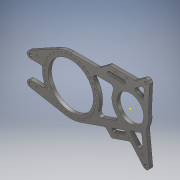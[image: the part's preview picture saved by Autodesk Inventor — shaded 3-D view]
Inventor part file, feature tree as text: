
AUTODESK INVENTOR PART (.ipt)
format: ipt  version: 2019 (Build 230136000, 136)  size: 542,208 bytes
history: native  units: in
note: dims shown in document units (in); Inventor stores cm internally (conversion verified against a paired STEP export)
features: sketch x20, extrude x14, hole x5, fillet x2, chamfer x1, projected_geometry x1
ambient origin geometry x8: Origin, YZ Plane, XZ Plane, XY Plane, X Axis, Y Axis, Z Axis, Center Point
bodies: Body1 (feature_tree)
feature tree (43):
  extrude  "Extrusion13"  Depth=0.5in TaperAngle=0.0deg
  hole  "Hole4"  [1 undecoded]
  extrude  "Extrusion14"  Depth=0.5in TaperAngle=0.0deg
  extrude  "Extrusion15"  Depth=5.0in
  extrude  "Extrusion16"  Depth=1.0in
  hole  "Hole6"  [1 undecoded]
  extrude  "Extrusion17"  Depth=0.5in TaperAngle=0.0deg
  hole  "Hole7"  [1 undecoded]
  hole  "Hole9"  [1 undecoded]
  hole  "Hole10"  [1 undecoded]
  extrude  "Extrusion18"  Depth=1.0in
  extrude  "Extrusion19"  Depth=1.0in
  sketch  "Sketch33"  dims[d183=0.257in d184=0.75in d185=0.438in d186=0.25in d187=0.5635in d188=1.0in d189=0.8108in d191=1.0in]
  extrude  "Extrusion21"  Depth=0.239in
  extrude  "Extrusion22"  Depth=0.5in
  extrude  "Extrusion23"  Depth=1.0in
  extrude  "Extrusion24"  Depth=0.75in
  fillet  "Fillet2"  Radius=0.75in
  extrude  "Extrusion25"  Depth=0.25in
  extrude  "Extrusion26"  Depth=1.0in TaperAngle=0.0deg
  fillet  "Fillet3"  Radius=0.25in
  extrude  "Extrusion27"  Depth=1.0in TaperAngle=0.0deg
  chamfer  "Chamfer1"  Distance=0.75in
  sketch  "Sketch40"  dims[d214=0.5in d215=1.0in d216=0.0in d217=0.25in d218=1.0in d219=0.0in d220=0.75in d221=0.5in d223=0.75in d231=0.25in d232=1.0in d233=0.0in d234=0.25in d235=1.0in d236=0.0in d237=0.75in d238=1.0in d239=0.0in d240=0.5in d241=0.5in d242=1.0in d243=0.0in d244=0.25in d247=0.75in d249=0.75in d250=0.5in d251=2.8in d252=0.375in d253=1.25in d255=0.75in d256=0.75in d257=1.0in d258=0.0in d259=0.25in d260=1.0in d261=0.0in d262=0.25in d263=0.5in d264=1.0in d265=0.0in d266=0.0156in d267=0.125in d268=45.0deg]
  sketch  "Sketch14"  dims[d96=8.5in d97=2.16in d98=9.0in d99=5.5in d100=1.0in d101=1.0in d102=6.0in d103=6.0in d104=3.718in d105=1.0in d108=10.718in d109=1.5in d111=0.5in d112=0.0in]
  sketch  "Sketch15"  dims[d113=0.386in d114=0.75in d115=0.762in d116=0.25in d117=0.5635in d118=0.484in d119=0.8108in d120=4.0in]
  sketch  "Sketch16"  dims[d121=6.75in d122=0.5in d123=0.0in]
  sketch  "Sketch18"  dims[d132=5.0in d133=17.223in]
  sketch  "Sketch19"  dims[d134=1.0in d135=1.0in]
  sketch  "Sketch20"  dims[d136=0.5in d137=0.0in d138=1.0in]
  sketch  "Sketch21"  dims[d140=4.0in d141=0.5in d142=0.0in]
  sketch  "Sketch23"  dims[d143=1.0in d144=1.625in]
  sketch  "Sketch27"  dims[d145=0.177in d146=0.75in d147=0.332in d148=0.25in d149=0.5635in d150=0.484in d151=0.8108in d155=1.0in d156=0.0in]
  sketch  "Sketch29"  dims[d157=1.625in]
  sketch  "Sketch31"  dims[d159=0.177in d160=0.75in d161=0.332in d162=0.25in d163=0.5635in d164=1.0in d165=0.8108in d178=7.75in]
  sketch  "Sketch32"  dims[d179=3.5433in d181=360.0deg]
  sketch  "Sketch34"  dims[d192=0.0481in d193=1.0in]
  sketch  "Sketch35"  dims[d194=0.3526in d197=0.239in]
  sketch  "Sketch36"  dims[d198=0.1195in d199=0.5in]
  sketch  "Sketch37"  dims[d200=0.266in d201=0.75in d202=0.507in d203=0.25in d204=0.5635in d205=1.0in d206=0.8108in d207=0.1718in]
  sketch  "Sketch38"  dims[d208=15.0deg d210=0.75in d211=0.75in]
  sketch  "Sketch39"  dims[d212=0.75in d213=0.25in]
  projected_geometry  "Project Cut Edges1"
note: 5 required parameter values undecoded (feature->parameter linkage not recoverable at this tier; creation-order binding heuristic only, values carry confidence <= 0.55)
